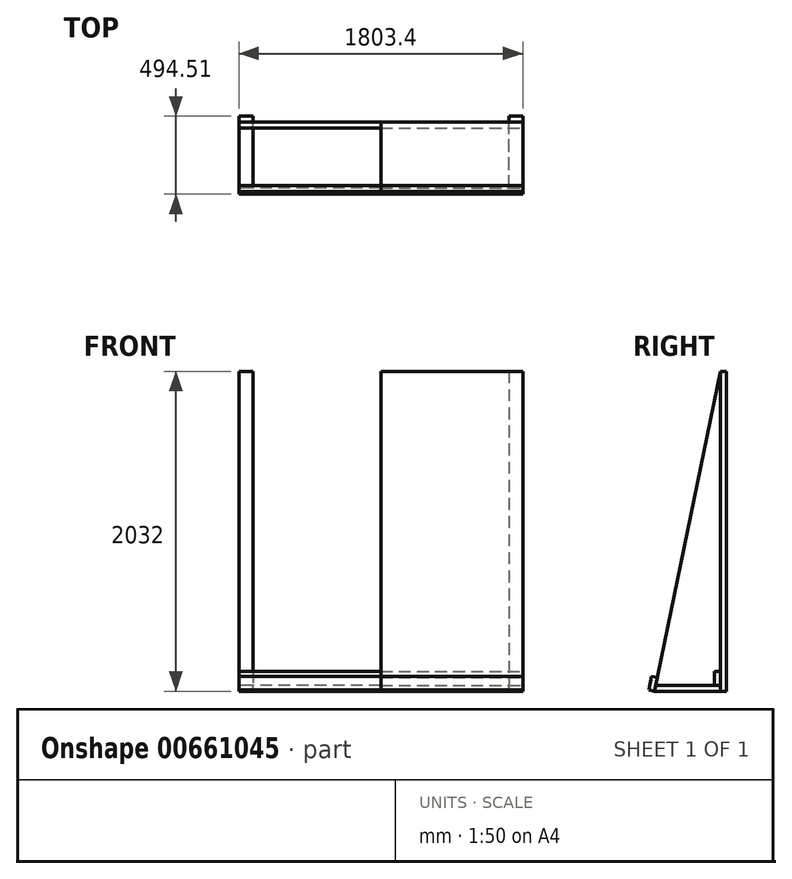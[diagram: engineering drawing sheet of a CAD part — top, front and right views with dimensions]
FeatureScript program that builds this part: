
annotation { "Feature Type Name" : "Feature", "Feature Type Description" : "" }
export const myFeature = defineFeature(function(context is Context, id is Id, definition is map)
    precondition{}
    {
        {
            var Q0;
            Q0=qCreatedBy(makeId("Right.planeOp"),FACE);
            var sketch = newSketch(context, id + "F0", { "sketchPlane" : qUnion([Q0])});
            skLineSegment(sketch, "E0", {"start": v(-209.55, 0) * mm, "end": v(209.55, 0) * mm});
            skLineSegment(sketch, "E1", {"start": v(209.55, 0) * mm, "end": v(209.55, 2032) * mm});
            skLineSegment(sketch, "E2", {"start": v(209.55, 2032) * mm, "end": v(-209.55, 0) * mm});
            skPoint(sketch, "E3", {"position": v(0, 0) * mm});
            skSolve(sketch);
        }
        {
            var Q0;
            Q0 = qSketchRegion(id + "F0", true);
            extrude(context, id + "F1", {"entities" : qUnion([Q0]), "depth" : 901.7 * mm, "offsetDistance" : 25.4 * mm});
        }
        {
            var Q0;
            Q0=makeQuery(id+"F1.opExtrude","CAP_EDGE",EDGE,{"disambiguationData":[OSD([sQuery(id+"F0.wireOp",EDGE,"E2")])],"isStart":false});
            cPoint(context, id + "F2", {"entities" : qUnion([Q0]), "parameter" : 0.5});
        }
        {
            var Q0;
            Q0=makeQuery(id+"F1.opExtrude","CAP_EDGE",EDGE,{"disambiguationData":[OSD([sQuery(id+"F0.wireOp",EDGE,"E2")])],"isStart":false});
            var Q1;
            Q1 = qCreatedBy(id + "F2" ,VERTEX);
            cPlane(context, id + "F3", {"entities" : qUnion([Q0, Q1]), "cplaneType" : CPlaneType.LINE_POINT, "offset" : 25.4 * mm, "width" : 152.4 * mm, "height" : 152.4 * mm});
        }
        {
            var Q0;
            Q0=makeQuery(id+"F1.opExtrude","SWEPT_FACE",FACE,{"disambiguationData":[OSD([sQuery(id+"F0.wireOp",EDGE,"E0")])]});
            var sketch = newSketch(context, id + "F4", { "sketchPlane" : qUnion([Q0])});
            skLineSegment(sketch, "E4.bottom", {"start": v(901.7, -209.55) * mm, "end": v(901.7, -247.65) * mm});
            skLineSegment(sketch, "E4.top", {"start": v(812.8, -209.55) * mm, "end": v(812.8, -247.65) * mm});
            skLineSegment(sketch, "E4.left", {"start": v(901.7, -209.55) * mm, "end": v(812.8, -209.55) * mm});
            skLineSegment(sketch, "E4.right", {"start": v(901.7, -247.65) * mm, "end": v(812.8, -247.65) * mm});
            skSolve(sketch);
        }
        {
            var Q0;
            Q0 = qSketchRegion(id + "F4", true);
            var Q1;
            Q1=makeQuery(id+"F1.opExtrude","CAP_VERTEX",VERTEX,{"disambiguationData":[OSD([sQuery(id+"F0.wireOp",EDGE,"E1"),sQuery(id+"F0.wireOp",EDGE,"E2")])],"isStart":false});
            extrude(context, id + "F5", {"entities" : qUnion([Q0]), "endBound" : BoundingType.UP_TO_VERTEX, "oppositeDirection" : true, "depth" : 215.9 * mm, "endBoundEntityVertex" : qUnion([Q1]), "offsetDistance" : 25.4 * mm});
        }
        {
            var Q0;
            Q0=qCreatedBy(id+"F3.planeOp",FACE);
            var sketch = newSketch(context, id + "F6", { "sketchPlane" : qUnion([Q0])});
            skLineSegment(sketch, "E5.bottom", {"start": v(812.8, 167.13) * mm, "end": v(812.8, 205.23) * mm});
            skLineSegment(sketch, "E5.top", {"start": v(901.7, 167.13) * mm, "end": v(901.7, 205.23) * mm});
            skLineSegment(sketch, "E5.left", {"start": v(812.8, 167.13) * mm, "end": v(901.7, 167.13) * mm});
            skLineSegment(sketch, "E5.right", {"start": v(812.8, 205.23) * mm, "end": v(901.7, 205.23) * mm});
            skPoint(sketch, "E6.0", {"position": v(901.7, 205.23) * mm});
            skSolve(sketch);
        }
        {
            var Q0;
            Q0 = qSketchRegion(id + "F6", true);
            var Q1;
            Q1=makeQuery(id+"F1.opExtrude","CAP_EDGE",EDGE,{"disambiguationData":[OSD([sQuery(id+"F0.wireOp",EDGE,"E2")])],"isStart":false});
            sweep(context, id + "F7", {"profiles" : qUnion([Q0]), "path" : qUnion([Q1])});
        }
        {
            var Q0;
            Q0=makeQuery(id+"F5.opExtrude","SWEPT_FACE",FACE,{"disambiguationData":[OSD([sQuery(id+"F4.wireOp",EDGE,"E4.left")])]});
            var sketch = newSketch(context, id + "F8", { "sketchPlane" : qUnion([Q0])});
            skLineSegment(sketch, "E7.bottom", {"start": v(901.7, 38.1) * mm, "end": v(901.7, 0) * mm});
            skLineSegment(sketch, "E7.top", {"start": v(812.8, 38.1) * mm, "end": v(812.8, 0) * mm});
            skLineSegment(sketch, "E7.left", {"start": v(901.7, 38.1) * mm, "end": v(812.8, 38.1) * mm});
            skLineSegment(sketch, "E7.right", {"start": v(901.7, 0) * mm, "end": v(812.8, 0) * mm});
            skSolve(sketch);
        }
        {
            var Q0;
            Q0 = qSketchRegion(id + "F8", true);
            var Q1;
            Q1=makeQuery(id+"F1.opExtrude","SWEPT_FACE",FACE,{"disambiguationData":[OSD([sQuery(id+"F0.wireOp",EDGE,"E2")])]});
            extrude(context, id + "F9", {"entities" : qUnion([Q0]), "endBound" : BoundingType.UP_TO_SURFACE, "depth" : 25.4 * mm, "endBoundEntityFace" : qUnion([Q1]), "offsetDistance" : 25.4 * mm});
        }
        {
            var Q0;
            Q0=makeQuery(id+"F5.opExtrude","SWEPT_BODY",BODY,{"disambiguationData":[OSD([sQuery(id+"F4.wireOp",EDGE,"E4.bottom"),sQuery(id+"F4.wireOp",EDGE,"E4.top"),sQuery(id+"F4.wireOp",EDGE,"E4.left"),sQuery(id+"F4.wireOp",EDGE,"E4.right")])]});
            var Q1;
            Q1=makeQuery(id+"F9.opExtrude","SWEPT_BODY",BODY,{"disambiguationData":[OSD([sQuery(id+"F8.wireOp",EDGE,"E7.bottom"),sQuery(id+"F8.wireOp",EDGE,"E7.top"),sQuery(id+"F8.wireOp",EDGE,"E7.left"),sQuery(id+"F8.wireOp",EDGE,"E7.right")])]});
            var Q2;
            Q2=makeQuery(id+"F7.opSweep","SWEPT_BODY",BODY,{"disambiguationData":[OSD([sQuery(id+"F0.wireOp",EDGE,"E2"),sQuery(id+"F6.wireOp",EDGE,"E5.bottom"),sQuery(id+"F6.wireOp",EDGE,"E5.top"),sQuery(id+"F6.wireOp",EDGE,"E5.left"),sQuery(id+"F6.wireOp",EDGE,"E5.right")])]});
            booleanBodies(context, id + "F10", {"operationType" : BooleanOperationType.SUBTRACTION, "tools" : qUnion([Q0, Q1]), "targets" : qUnion([Q2]), "keepTools" : true});
        }
        {
            var Q0;
            Q0=makeQuery(id+"F10.opBoolean","SPLIT",BODY,{"disambiguationData":[OD(0.0)],"derivedFrom":makeQuery(id+"F7.opSweep","SWEPT_BODY",BODY,{"disambiguationData":[OSD([sQuery(id+"F0.wireOp",EDGE,"E2"),sQuery(id+"F6.wireOp",EDGE,"E5.bottom"),sQuery(id+"F6.wireOp",EDGE,"E5.top"),sQuery(id+"F6.wireOp",EDGE,"E5.left"),sQuery(id+"F6.wireOp",EDGE,"E5.right")])]})});
            deleteBodies(context, id + "F11", {"entities" : qUnion([Q0])});
        }
        {
            var Q0;
            Q0=makeQuery(id+"F1.opExtrude","CAP_FACE",FACE,{"disambiguationData":[OSD([sQuery(id+"F0.wireOp",EDGE,"E0"),sQuery(id+"F0.wireOp",EDGE,"E1"),sQuery(id+"F0.wireOp",EDGE,"E2")])],"isStart":false});
            var sketch = newSketch(context, id + "F12", { "sketchPlane" : qUnion([Q0])});
            skLineSegment(sketch, "E8.bottom", {"start": v(-209.55, 0) * mm, "end": v(-246.86, 7.7) * mm});
            skLineSegment(sketch, "E8.top", {"start": v(-191.6, 87.07) * mm, "end": v(-228.9, 94.76) * mm});
            skLineSegment(sketch, "E8.left", {"start": v(-209.55, 0) * mm, "end": v(-191.6, 87.07) * mm});
            skLineSegment(sketch, "E8.right", {"start": v(-246.86, 7.7) * mm, "end": v(-228.9, 94.76) * mm});
            skLineSegment(sketch, "E9.bottom", {"start": v(209.55, 38.1) * mm, "end": v(171.45, 38.1) * mm});
            skLineSegment(sketch, "E9.top", {"start": v(209.55, 127) * mm, "end": v(171.45, 127) * mm});
            skLineSegment(sketch, "E9.left", {"start": v(209.55, 38.1) * mm, "end": v(209.55, 127) * mm});
            skLineSegment(sketch, "E9.right", {"start": v(171.45, 38.1) * mm, "end": v(171.45, 127) * mm});
            skSolve(sketch);
        }
        {
            var Q0;
            Q0 = qSketchRegion(id + "F12", true);
            var Q1;
            Q1=makeQuery(id+"F1.opExtrude","CAP_FACE",FACE,{"disambiguationData":[OSD([sQuery(id+"F0.wireOp",EDGE,"E0"),sQuery(id+"F0.wireOp",EDGE,"E1"),sQuery(id+"F0.wireOp",EDGE,"E2")])],"isStart":true});
            extrude(context, id + "F13", {"entities" : qUnion([Q0]), "endBound" : BoundingType.UP_TO_SURFACE, "oppositeDirection" : true, "depth" : 25.4 * mm, "endBoundEntityFace" : qUnion([Q1]), "offsetDistance" : 25.4 * mm});
        }
        {
            var Q0;
            Q0=makeQuery(id+"F10.opBoolean","SPLIT",BODY,{"disambiguationData":[OD(1.0)],"derivedFrom":makeQuery(id+"F7.opSweep","SWEPT_BODY",BODY,{"disambiguationData":[OSD([sQuery(id+"F0.wireOp",EDGE,"E2"),sQuery(id+"F6.wireOp",EDGE,"E5.bottom"),sQuery(id+"F6.wireOp",EDGE,"E5.top"),sQuery(id+"F6.wireOp",EDGE,"E5.left"),sQuery(id+"F6.wireOp",EDGE,"E5.right")])]})});
            var Q1;
            Q1=makeQuery(id+"F5.opExtrude","SWEPT_BODY",BODY,{"disambiguationData":[OSD([sQuery(id+"F4.wireOp",EDGE,"E4.bottom"),sQuery(id+"F4.wireOp",EDGE,"E4.top"),sQuery(id+"F4.wireOp",EDGE,"E4.left"),sQuery(id+"F4.wireOp",EDGE,"E4.right")])]});
            var Q2;
            Q2=makeQuery(id+"FZm3evDw3ylXZA0_6.opExtrude","SWEPT_BODY",BODY,{"disambiguationData":[OSD([sQuery(id+"FBfVjYJmLMIwhJ8_6.wireOp",EDGE,"0678d4ec-2984-4bdf-8824-ebb49076f04a.bottom"),sQuery(id+"FBfVjYJmLMIwhJ8_6.wireOp",EDGE,"0678d4ec-2984-4bdf-8824-ebb49076f04a.top"),sQuery(id+"FBfVjYJmLMIwhJ8_6.wireOp",EDGE,"0678d4ec-2984-4bdf-8824-ebb49076f04a.left"),sQuery(id+"FBfVjYJmLMIwhJ8_6.wireOp",EDGE,"0678d4ec-2984-4bdf-8824-ebb49076f04a.right")])]});
            var Q3;
            Q3=makeQuery(id+"F9.opExtrude","SWEPT_BODY",BODY,{"disambiguationData":[OSD([sQuery(id+"F8.wireOp",EDGE,"E7.bottom"),sQuery(id+"F8.wireOp",EDGE,"E7.top"),sQuery(id+"F8.wireOp",EDGE,"E7.left"),sQuery(id+"F8.wireOp",EDGE,"E7.right")])]});
            var Q4;
            Q4=makeQuery(id+"F13.opExtrude","SWEPT_BODY",BODY,{"disambiguationData":[OSD([sQuery(id+"F12.wireOp",EDGE,"E9.bottom"),sQuery(id+"F12.wireOp",EDGE,"E9.top"),sQuery(id+"F12.wireOp",EDGE,"E9.left"),sQuery(id+"F12.wireOp",EDGE,"E9.right")])]});
            var Q5;
            Q5=makeQuery(id+"F13.opExtrude","SWEPT_BODY",BODY,{"disambiguationData":[OSD([sQuery(id+"F12.wireOp",EDGE,"E8.bottom"),sQuery(id+"F12.wireOp",EDGE,"E8.top"),sQuery(id+"F12.wireOp",EDGE,"E8.left"),sQuery(id+"F12.wireOp",EDGE,"E8.right")])]});
            var Q6;
            Q6=makeQuery(id+"F1.opExtrude","CAP_FACE",FACE,{"disambiguationData":[OSD([sQuery(id+"F0.wireOp",EDGE,"E0"),sQuery(id+"F0.wireOp",EDGE,"E1"),sQuery(id+"F0.wireOp",EDGE,"E2")])],"isStart":true});
            mirror(context, id + "F14", {"entities" : qUnion([Q0, Q1, Q2, Q3, Q4, Q5]), "mirrorPlane" : qUnion([Q6])});
        }
    });
